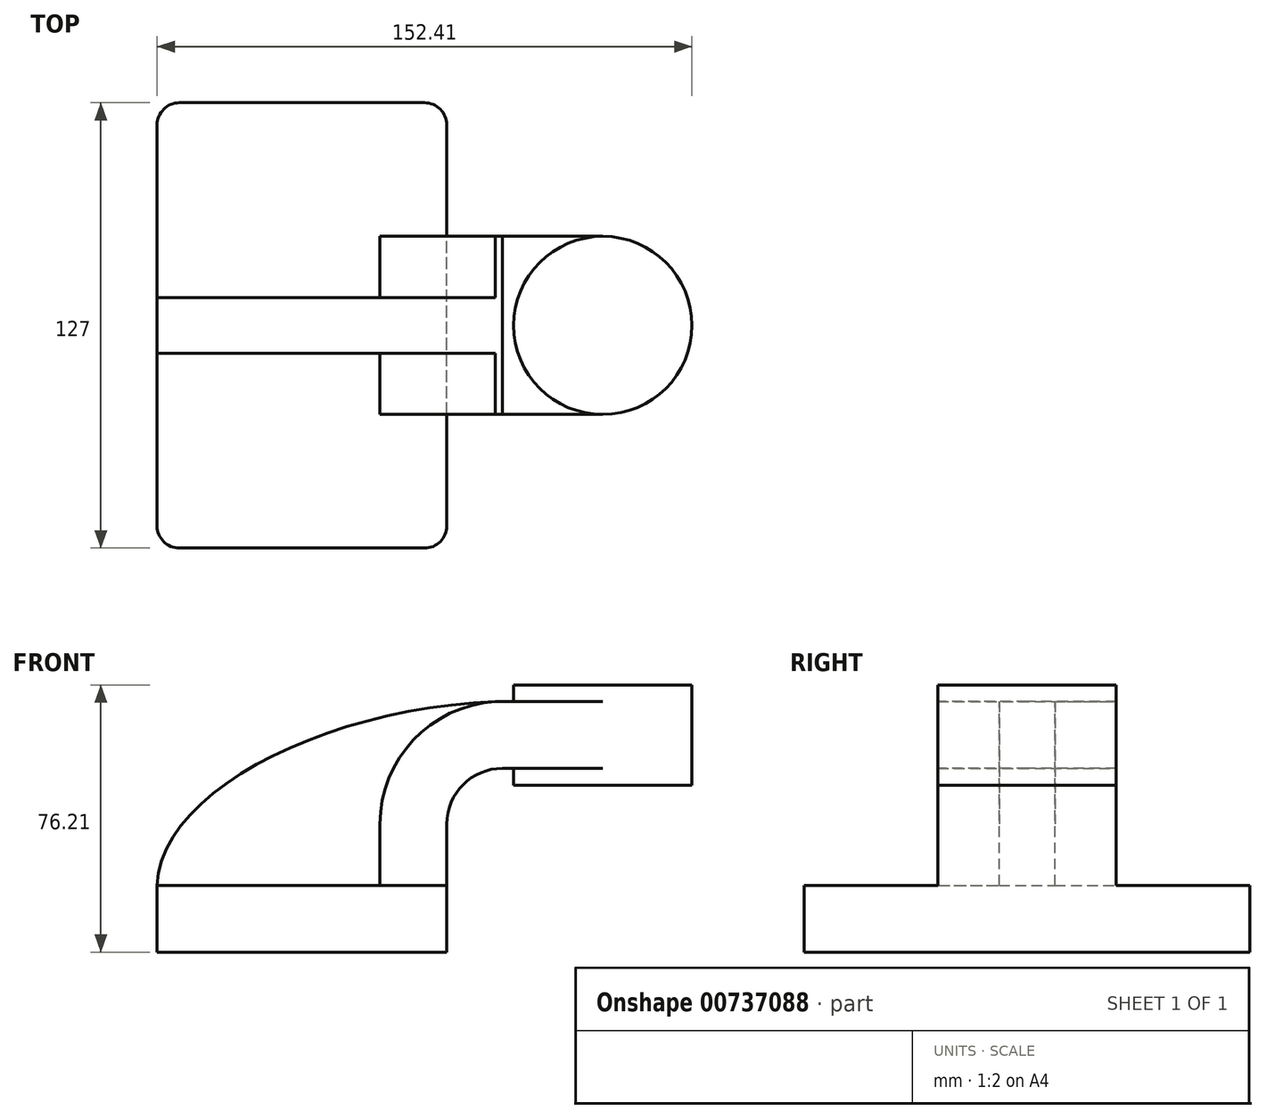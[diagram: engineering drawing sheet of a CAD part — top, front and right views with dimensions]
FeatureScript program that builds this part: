
annotation { "Feature Type Name" : "Feature", "Feature Type Description" : "" }
export const myFeature = defineFeature(function(context is Context, id is Id, definition is map)
    precondition{}
    {
        {
            var Q0;
            Q0=qCreatedBy(makeId("Front.planeOp"),FACE);
            var sketch = newSketch(context, id + "F0", { "sketchPlane" : qUnion([Q0])});
            skLineSegment(sketch, "E0.bottom", {"start": v(-41.28, -9.53) * mm, "end": v(41.28, -9.53) * mm});
            skLineSegment(sketch, "E0.top", {"start": v(-41.28, 9.53) * mm, "end": v(41.28, 9.53) * mm});
            skLineSegment(sketch, "E0.left", {"start": v(-41.28, -9.53) * mm, "end": v(-41.28, 9.53) * mm});
            skLineSegment(sketch, "E0.right", {"start": v(41.28, -9.53) * mm, "end": v(41.28, 9.53) * mm});
            skPoint(sketch, "E0.middle", {"position": v(0, 0) * mm});
            skLineSegment(sketch, "E1.bottom", {"start": v(60.32, 38.1) * mm, "end": v(111.12, 38.1) * mm});
            skLineSegment(sketch, "E1.top", {"start": v(60.32, 66.68) * mm, "end": v(111.12, 66.68) * mm});
            skLineSegment(sketch, "E1.left", {"start": v(60.32, 38.1) * mm, "end": v(60.32, 66.68) * mm});
            skLineSegment(sketch, "E1.right", {"start": v(111.12, 38.1) * mm, "end": v(111.12, 66.68) * mm});
            skPoint(sketch, "E1.middle", {"position": v(85.72, 52.39) * mm});
            skLineSegment(sketch, "E2", {"start": v(41.28, 9.53) * mm, "end": v(41.28, 27) * mm});
            skArc(sketch, "E3", {"start": v(41.27, 27) * mm, "mid": v(45.92, 38.23) * mm, "end": v(57.15, 42.88) * mm});
            skLineSegment(sketch, "E4", {"start": v(57.15, 42.88) * mm, "end": v(85.72, 42.88) * mm});
            skLineSegment(sketch, "E5.0", {"start": v(57.15, 61.93) * mm, "end": v(85.72, 61.93) * mm});
            skArc(sketch, "E5.1", {"start": v(22.23, 27) * mm, "mid": v(32.45, 51.7) * mm, "end": v(57.15, 61.93) * mm});
            skLineSegment(sketch, "E5.2", {"start": v(22.22, 9.53) * mm, "end": v(22.22, 27) * mm});
            skFitSpline(sketch, "E6", {"points": [v(-41.28, 9.53) * mm, v(57.15, 61.93) * mm], "startDerivative": vector(2.92, 82.55) * mm, "endDerivative": vector(145.6, 3.36) * mm});
            skLineSegment(sketch, "E7", {"start": v(85.72, 38.1) * mm, "end": v(85.72, 66.68) * mm});
            skSolve(sketch);
        }
        {
            var Q0;
            Q0=makeQuery(id+"F0.imprint","IMPRINT",FACE,{"disambiguationData":[TD([[makeQuery(id+"F0.imprint","IMPRINT",EDGE,{"derivedFrom":sQuery(id+"F0.wireOp",EDGE,"E0.bottom")}),1.0]])]});
            extrude(context, id + "F1", {"entities" : qUnion([Q0]), "endBound" : BoundingType.SYMMETRIC, "depth" : 127 * mm, "offsetDistance" : 25.4 * mm});
        }
        {
            var Q0;
            {var subQ1=sQuery(id+"F0.wireOp",EDGE,"E2");Q0=makeQuery(id+"F0.imprint","IMPRINT",FACE,{"disambiguationData":[TD([[makeQuery(id+"F0.imprint","IMPRINT",EDGE,{"derivedFrom":subQ1}),1.0]])]});}
            var Q1;
            {var subQ0=sQuery(id+"F0.wireOp",EDGE,"E4");var subQ1=sQuery(id+"F0.wireOp",EDGE,"E1.left");var subQ2=makeQuery(id+"F0.imprint","INTERSECT",VERTEX,{"derivedFrom":[subQ1,subQ0]});Q1=makeQuery(id+"F0.imprint","IMPRINT",FACE,{"disambiguationData":[TD([[makeQuery(id+"F0.imprint","IMPRINT",EDGE,{"disambiguationData":[TD([[subQ2,-1.0]])],"derivedFrom":subQ1}),-1.0]])]});}
            extrude(context, id + "F2", {"entities" : qUnion([Q0, Q1]), "operationType" : NewBodyOperationType.ADD, "endBound" : BoundingType.SYMMETRIC, "depth" : 50.8 * mm, "offsetDistance" : 25.4 * mm});
        }
        {
            var Q0;
            {var subQ3=sQuery(id+"F0.wireOp",EDGE,"E5.2");Q0=makeQuery(id+"F0.imprint","IMPRINT",FACE,{"disambiguationData":[TD([[makeQuery(id+"F0.imprint","IMPRINT",EDGE,{"derivedFrom":subQ3}),1.0]])]});}
            extrude(context, id + "F3", {"entities" : qUnion([Q0]), "operationType" : NewBodyOperationType.ADD, "endBound" : BoundingType.SYMMETRIC, "depth" : 15.88 * mm, "offsetDistance" : 25.4 * mm});
        }
        {
            var Q0;
            {var subQ4=sQuery(id+"F0.wireOp",EDGE,"E1.right");Q0=makeQuery(id+"F0.imprint","IMPRINT",FACE,{"disambiguationData":[TD([[makeQuery(id+"F0.imprint","IMPRINT",EDGE,{"derivedFrom":subQ4}),1.0]])]});}
            var Q1;
            Q1=sQuery(id+"F0.wireOp",EDGE,"E7");
            revolve(context, id + "F4", {"operationType" : NewBodyOperationType.ADD, "surfaceOperationType" : NewSurfaceOperationType.NEW, "entities" : qUnion([Q0]), "axis" : qUnion([Q1]), "revolveType" : RevolveType.FULL});
        }
        {
            var Q0;
            Q0=makeQuery(id+"F1.opExtrude","CAP_EDGE",EDGE,{"disambiguationData":[OSD([sQuery(id+"F0.wireOp",EDGE,"E0.left")])],"isStart":true});
            var Q1;
            Q1=makeQuery(id+"F1.opExtrude","CAP_EDGE",EDGE,{"disambiguationData":[OSD([sQuery(id+"F0.wireOp",EDGE,"E0.right")])],"isStart":true});
            var Q2;
            Q2=makeQuery(id+"F1.opExtrude","CAP_EDGE",EDGE,{"disambiguationData":[OSD([sQuery(id+"F0.wireOp",EDGE,"E0.right")])],"isStart":false});
            var Q3;
            Q3=makeQuery(id+"F1.opExtrude","CAP_EDGE",EDGE,{"disambiguationData":[OSD([sQuery(id+"F0.wireOp",EDGE,"E0.left")])],"isStart":false});
            fillet(context, id + "F5", {"entities" : qUnion([Q0, Q1, Q2, Q3]), "radius" : 6.35 * mm, "tangentPropagation" : true, "allowEdgeOverflow" : false});
        }
    });
